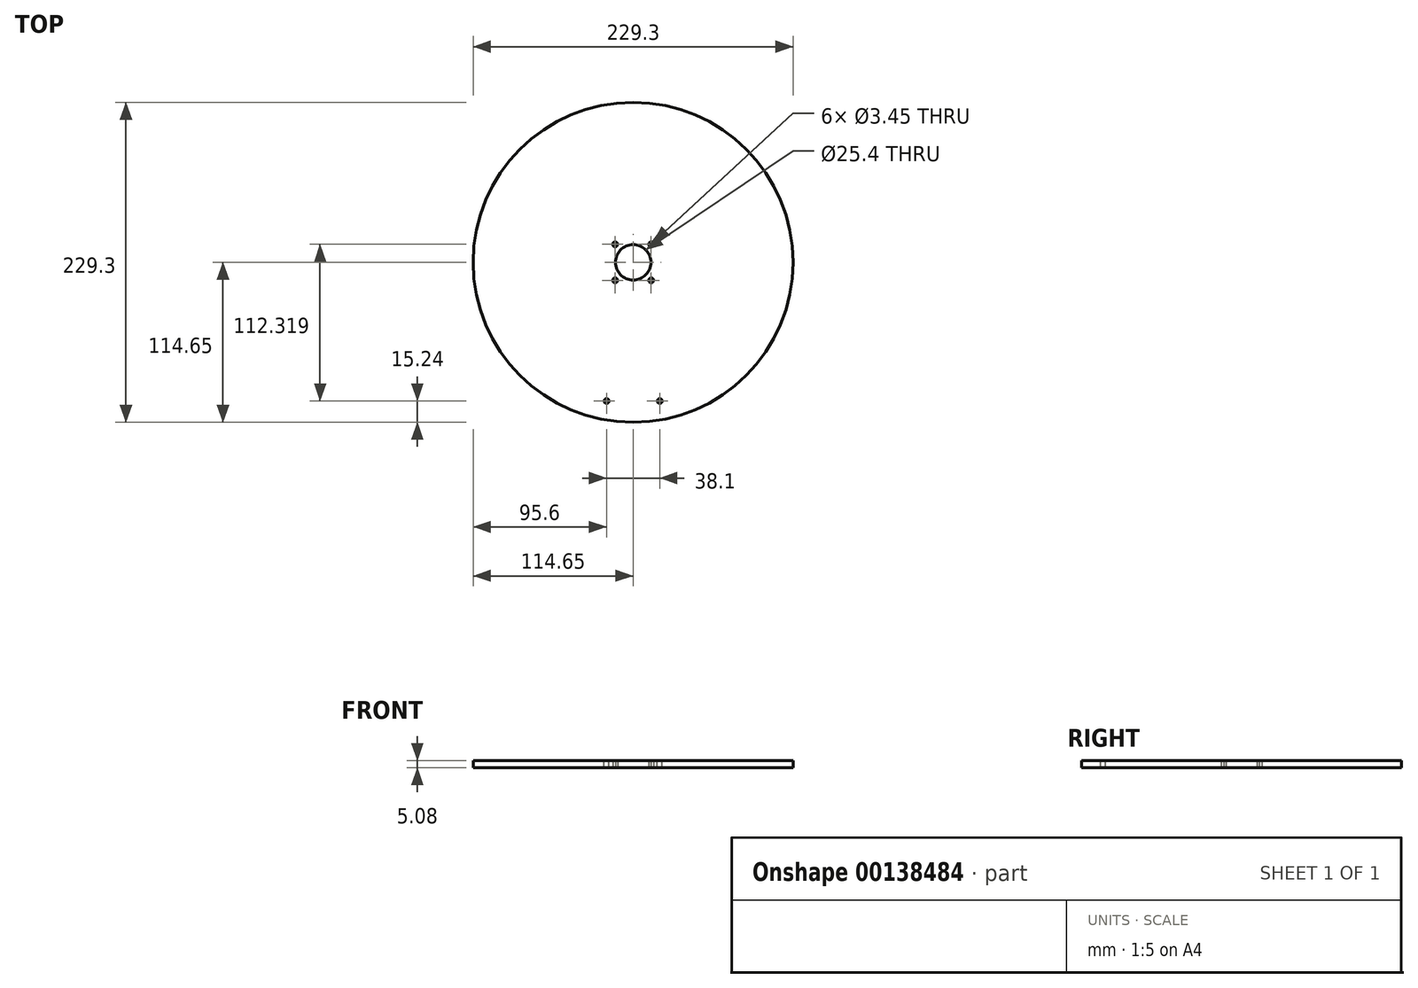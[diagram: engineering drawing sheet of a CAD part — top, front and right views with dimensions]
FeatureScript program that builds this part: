
annotation { "Feature Type Name" : "Feature", "Feature Type Description" : "" }
export const myFeature = defineFeature(function(context is Context, id is Id, definition is map)
    precondition{}
    {
        {
            var Q0;
            Q0=qCreatedBy(makeId("Top.planeOp"),FACE);
            var sketch = newSketch(context, id + "F0", { "sketchPlane" : qUnion([Q0])});
            skCircle(sketch, "E0", {"center": v(0, 0) * mm, "radius": 114.65 * mm});
            skCircle(sketch, "E1", {"center": v(0, 0) * mm, "radius": 12.7 * mm});
            skCircle(sketch, "E2", {"center": v(0, 0) * mm, "radius": 14.29 * mm, "construction": true});
            skLineSegment(sketch, "E3.bottom", {"start": v(-12.9, 12.9) * mm, "end": v(12.9, 12.9) * mm, "construction": true});
            skLineSegment(sketch, "E3.top", {"start": v(-12.9, -12.9) * mm, "end": v(12.9, -12.9) * mm, "construction": true});
            skLineSegment(sketch, "E3.left", {"start": v(-12.9, 12.9) * mm, "end": v(-12.9, -12.9) * mm, "construction": true});
            skLineSegment(sketch, "E3.right", {"start": v(12.9, 12.9) * mm, "end": v(12.9, -12.9) * mm, "construction": true});
            skCircle(sketch, "E4", {"center": v(-12.9, 12.9) * mm, "radius": 3.97 * mm, "construction": true});
            skCircle(sketch, "E5", {"center": v(-12.9, 12.9) * mm, "radius": 1.73 * mm});
            skCircle(sketch, "E6", {"center": v(12.9, 12.9) * mm, "radius": 1.73 * mm});
            skCircle(sketch, "E7", {"center": v(12.9, -12.9) * mm, "radius": 1.73 * mm});
            skCircle(sketch, "E8", {"center": v(-12.9, -12.9) * mm, "radius": 1.73 * mm});
            skSolve(sketch);
        }
        {
            var Q0;
            Q0 = qSketchRegion(id + "F0", true);
            extrude(context, id + "F1", {"entities" : qUnion([Q0]), "depth" : 5.08 * mm});
        }
        {
            var Q0;
            Q0=makeQuery(id+"F1.opExtrude","CAP_FACE",FACE,{"disambiguationData":[OSD([sQuery(id+"F0.wireOp",EDGE,"E0")])],"isStart":false});
            var sketch = newSketch(context, id + "F2", { "sketchPlane" : qUnion([Q0])});
            skLineSegment(sketch, "E9", {"start": v(0, 0) * mm, "end": v(0, -99.4) * mm, "construction": true});
            skLineSegment(sketch, "E10", {"start": v(-19.05, -99.4) * mm, "end": v(19.05, -99.4) * mm, "construction": true});
            skCircle(sketch, "E11", {"center": v(0, -99.4) * mm, "radius": 15.24 * mm, "construction": true});
            skCircle(sketch, "E12", {"center": v(19.05, -99.4) * mm, "radius": 1.73 * mm});
            skCircle(sketch, "E13", {"center": v(-19.05, -99.4) * mm, "radius": 1.73 * mm});
            skSolve(sketch);
        }
        {
            var Q0;
            Q0 = qSketchRegion(id + "F2", true);
            var Q1;
            Q1=makeQuery(id+"F1.opExtrude","CAP_FACE",FACE,{"disambiguationData":[OSD([sQuery(id+"F0.wireOp",EDGE,"E0")])],"isStart":true});
            extrude(context, id + "F3", {"entities" : qUnion([Q0]), "operationType" : NewBodyOperationType.REMOVE, "endBound" : BoundingType.UP_TO_SURFACE, "oppositeDirection" : true, "endBoundEntityFace" : qUnion([Q1]), "depth" : 25.4 * mm});
        }
    });
